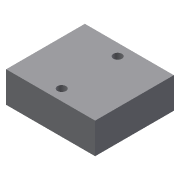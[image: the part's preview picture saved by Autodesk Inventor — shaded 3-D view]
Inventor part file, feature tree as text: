
AUTODESK INVENTOR PART (.ipt)
format: ipt  version: 2013 (Build 170138000, 138)  size: 79,360 bytes
history: native  units: in
note: dims shown in document units (in); Inventor stores cm internally (conversion verified against a paired STEP export)
features: sketch x2, extrude x1, hole x1
ambient origin geometry x8: Origin, YZ Plane, XZ Plane, XY Plane, X Axis, Y Axis, Z Axis, Center Point
bodies: Solid1 (feature_tree)
feature tree (4):
  extrude  "Extrusion1"  Depth=2.3in
  hole  "Hole1"  [1 undecoded]
  sketch  "Sketch1"  dims[d0=2.6in d1=2.3in]
  sketch  "Sketch2"  dims[d2=0.9in d3=0.0in d4=0.25in d5=0.75in d6=0.375in d7=0.25in d8=0.5635in d9=1.0in d10=0.8108in d11=0.0in]
note: 1 required parameter value undecoded (feature->parameter linkage not recoverable at this tier; creation-order binding heuristic only, values carry confidence <= 0.55)
